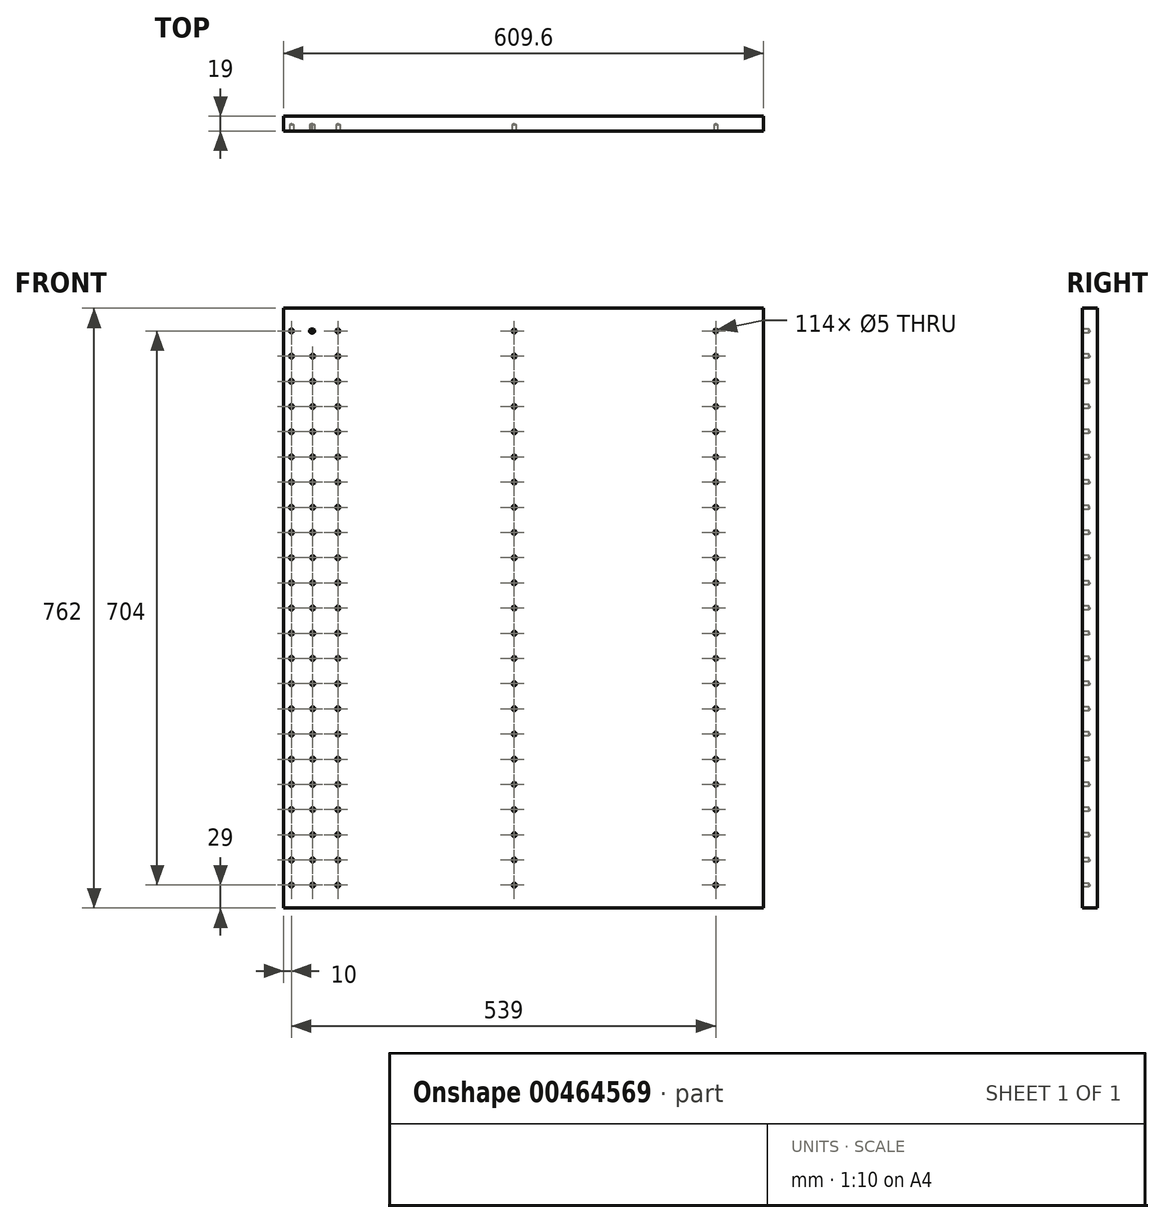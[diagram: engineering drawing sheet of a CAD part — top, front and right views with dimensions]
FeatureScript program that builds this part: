
annotation { "Feature Type Name" : "Feature", "Feature Type Description" : "" }
export const myFeature = defineFeature(function(context is Context, id is Id, definition is map)
    precondition{}
    {
        {
            var Q0;
            Q0=qCreatedBy(makeId("Front.planeOp"),FACE);
            var sketch = newSketch(context, id + "F0", { "sketchPlane" : qUnion([Q0])});
            skLineSegment(sketch, "E0.bottom", {"start": v(304.8, 381) * mm, "end": v(-304.8, 381) * mm});
            skLineSegment(sketch, "E0.top", {"start": v(304.8, -381) * mm, "end": v(-304.8, -381) * mm});
            skLineSegment(sketch, "E0.left", {"start": v(304.8, 381) * mm, "end": v(304.8, -381) * mm});
            skLineSegment(sketch, "E0.right", {"start": v(-304.8, 381) * mm, "end": v(-304.8, -381) * mm});
            skPoint(sketch, "E0.middle", {"position": v(0, 0) * mm});
            skSolve(sketch);
        }
        {
            var Q0;
            Q0=makeQuery(id+"F0.imprint","IMPRINT",FACE,{"disambiguationData":[TD([[makeQuery(id+"F0.imprint","IMPRINT",EDGE,{"derivedFrom":sQuery(id+"F0.wireOp",EDGE,"E0.bottom")}),1.0]])]});
            extrude(context, id + "F1", {"entities" : qUnion([Q0]), "depth" : 19 * mm});
        }
        {
            var Q0;
            Q0=makeQuery(id+"F1.opExtrude","CAP_FACE",FACE,{"disambiguationData":[OSD([sQuery(id+"F0.wireOp",EDGE,"E0.bottom"),sQuery(id+"F0.wireOp",EDGE,"E0.top"),sQuery(id+"F0.wireOp",EDGE,"E0.left"),sQuery(id+"F0.wireOp",EDGE,"E0.right")])],"isStart":false});
            var sketch = newSketch(context, id + "F2", { "sketchPlane" : qUnion([Q0])});
            skCircle(sketch, "E1", {"center": v(-294.8, 352) * mm, "radius": 2.5 * mm});
            skCircle(sketch, "E2.1.0.0", {"center": v(-267.8, 352) * mm, "radius": 2.5 * mm});
            skLineSegment(sketch, "E2.direction1", {"start": v(-294.8, 352) * mm, "end": v(-267.8, 352) * mm, "construction": true});
            skCircle(sketch, "E3.1.0.0", {"center": v(-235.8, 352) * mm, "radius": 2.5 * mm});
            skLineSegment(sketch, "E3.direction1", {"start": v(-267.8, 352) * mm, "end": v(-235.8, 352) * mm, "construction": true});
            skCircle(sketch, "E4.1.0.0", {"center": v(-11.8, 352) * mm, "radius": 2.5 * mm});
            skLineSegment(sketch, "E4.direction1", {"start": v(-235.8, 352) * mm, "end": v(-11.8, 352) * mm, "construction": true});
            skCircle(sketch, "E5.1.0.0", {"center": v(244.2, 352) * mm, "radius": 2.5 * mm});
            skLineSegment(sketch, "E5.direction1", {"start": v(-11.8, 352) * mm, "end": v(244.2, 352) * mm, "construction": true});
            skCircle(sketch, "E6.0.1.0", {"center": v(-11.8, 320) * mm, "radius": 2.5 * mm});
            skCircle(sketch, "E6.0.1.1", {"center": v(244.2, 320) * mm, "radius": 2.5 * mm});
            skCircle(sketch, "E6.0.1.2", {"center": v(-267.8, 320) * mm, "radius": 2.5 * mm});
            skCircle(sketch, "E6.0.1.3", {"center": v(-235.8, 320) * mm, "radius": 2.5 * mm});
            skCircle(sketch, "E6.0.1.4", {"center": v(-294.8, 320) * mm, "radius": 2.5 * mm});
            skCircle(sketch, "E6.0.2.0", {"center": v(-11.8, 288) * mm, "radius": 2.5 * mm});
            skCircle(sketch, "E6.0.2.1", {"center": v(244.2, 288) * mm, "radius": 2.5 * mm});
            skCircle(sketch, "E6.0.2.2", {"center": v(-267.8, 288) * mm, "radius": 2.5 * mm});
            skCircle(sketch, "E6.0.2.3", {"center": v(-235.8, 288) * mm, "radius": 2.5 * mm});
            skCircle(sketch, "E6.0.2.4", {"center": v(-294.8, 288) * mm, "radius": 2.5 * mm});
            skCircle(sketch, "E6.0.3.0", {"center": v(-11.8, 256) * mm, "radius": 2.5 * mm});
            skCircle(sketch, "E6.0.3.1", {"center": v(244.2, 256) * mm, "radius": 2.5 * mm});
            skCircle(sketch, "E6.0.3.2", {"center": v(-267.8, 256) * mm, "radius": 2.5 * mm});
            skCircle(sketch, "E6.0.3.3", {"center": v(-235.8, 256) * mm, "radius": 2.5 * mm});
            skCircle(sketch, "E6.0.3.4", {"center": v(-294.8, 256) * mm, "radius": 2.5 * mm});
            skCircle(sketch, "E6.0.4.0", {"center": v(-11.8, 224) * mm, "radius": 2.5 * mm});
            skCircle(sketch, "E6.0.4.1", {"center": v(244.2, 224) * mm, "radius": 2.5 * mm});
            skCircle(sketch, "E6.0.4.2", {"center": v(-267.8, 224) * mm, "radius": 2.5 * mm});
            skCircle(sketch, "E6.0.4.3", {"center": v(-235.8, 224) * mm, "radius": 2.5 * mm});
            skCircle(sketch, "E6.0.4.4", {"center": v(-294.8, 224) * mm, "radius": 2.5 * mm});
            skCircle(sketch, "E6.0.5.0", {"center": v(-11.8, 192) * mm, "radius": 2.5 * mm});
            skCircle(sketch, "E6.0.5.1", {"center": v(244.2, 192) * mm, "radius": 2.5 * mm});
            skCircle(sketch, "E6.0.5.2", {"center": v(-267.8, 192) * mm, "radius": 2.5 * mm});
            skCircle(sketch, "E6.0.5.3", {"center": v(-235.8, 192) * mm, "radius": 2.5 * mm});
            skCircle(sketch, "E6.0.5.4", {"center": v(-294.8, 192) * mm, "radius": 2.5 * mm});
            skCircle(sketch, "E6.0.6.0", {"center": v(-11.8, 160) * mm, "radius": 2.5 * mm});
            skCircle(sketch, "E6.0.6.1", {"center": v(244.2, 160) * mm, "radius": 2.5 * mm});
            skCircle(sketch, "E6.0.6.2", {"center": v(-267.8, 160) * mm, "radius": 2.5 * mm});
            skCircle(sketch, "E6.0.6.3", {"center": v(-235.8, 160) * mm, "radius": 2.5 * mm});
            skCircle(sketch, "E6.0.6.4", {"center": v(-294.8, 160) * mm, "radius": 2.5 * mm});
            skCircle(sketch, "E6.0.7.0", {"center": v(-11.8, 128) * mm, "radius": 2.5 * mm});
            skCircle(sketch, "E6.0.7.1", {"center": v(244.2, 128) * mm, "radius": 2.5 * mm});
            skCircle(sketch, "E6.0.7.2", {"center": v(-267.8, 128) * mm, "radius": 2.5 * mm});
            skCircle(sketch, "E6.0.7.3", {"center": v(-235.8, 128) * mm, "radius": 2.5 * mm});
            skCircle(sketch, "E6.0.7.4", {"center": v(-294.8, 128) * mm, "radius": 2.5 * mm});
            skCircle(sketch, "E6.0.8.0", {"center": v(-11.8, 96) * mm, "radius": 2.5 * mm});
            skCircle(sketch, "E6.0.8.1", {"center": v(244.2, 96) * mm, "radius": 2.5 * mm});
            skCircle(sketch, "E6.0.8.2", {"center": v(-267.8, 96) * mm, "radius": 2.5 * mm});
            skCircle(sketch, "E6.0.8.3", {"center": v(-235.8, 96) * mm, "radius": 2.5 * mm});
            skCircle(sketch, "E6.0.8.4", {"center": v(-294.8, 96) * mm, "radius": 2.5 * mm});
            skCircle(sketch, "E6.0.9.0", {"center": v(-11.8, 64) * mm, "radius": 2.5 * mm});
            skCircle(sketch, "E6.0.9.1", {"center": v(244.2, 64) * mm, "radius": 2.5 * mm});
            skCircle(sketch, "E6.0.9.2", {"center": v(-267.8, 64) * mm, "radius": 2.5 * mm});
            skCircle(sketch, "E6.0.9.3", {"center": v(-235.8, 64) * mm, "radius": 2.5 * mm});
            skCircle(sketch, "E6.0.9.4", {"center": v(-294.8, 64) * mm, "radius": 2.5 * mm});
            skCircle(sketch, "E6.0.10.0", {"center": v(-11.8, 32) * mm, "radius": 2.5 * mm});
            skCircle(sketch, "E6.0.10.1", {"center": v(244.2, 32) * mm, "radius": 2.5 * mm});
            skCircle(sketch, "E6.0.10.2", {"center": v(-267.8, 32) * mm, "radius": 2.5 * mm});
            skCircle(sketch, "E6.0.10.3", {"center": v(-235.8, 32) * mm, "radius": 2.5 * mm});
            skCircle(sketch, "E6.0.10.4", {"center": v(-294.8, 32) * mm, "radius": 2.5 * mm});
            skCircle(sketch, "E6.0.11.0", {"center": v(-11.8, 0) * mm, "radius": 2.5 * mm});
            skCircle(sketch, "E6.0.11.1", {"center": v(244.2, 0) * mm, "radius": 2.5 * mm});
            skCircle(sketch, "E6.0.11.2", {"center": v(-267.8, 0) * mm, "radius": 2.5 * mm});
            skCircle(sketch, "E6.0.11.3", {"center": v(-235.8, 0) * mm, "radius": 2.5 * mm});
            skCircle(sketch, "E6.0.11.4", {"center": v(-294.8, 0) * mm, "radius": 2.5 * mm});
            skCircle(sketch, "E6.0.12.0", {"center": v(-11.8, -32) * mm, "radius": 2.5 * mm});
            skCircle(sketch, "E6.0.12.1", {"center": v(244.2, -32) * mm, "radius": 2.5 * mm});
            skCircle(sketch, "E6.0.12.2", {"center": v(-267.8, -32) * mm, "radius": 2.5 * mm});
            skCircle(sketch, "E6.0.12.3", {"center": v(-235.8, -32) * mm, "radius": 2.5 * mm});
            skCircle(sketch, "E6.0.12.4", {"center": v(-294.8, -32) * mm, "radius": 2.5 * mm});
            skCircle(sketch, "E6.0.13.0", {"center": v(-11.8, -64) * mm, "radius": 2.5 * mm});
            skCircle(sketch, "E6.0.13.1", {"center": v(244.2, -64) * mm, "radius": 2.5 * mm});
            skCircle(sketch, "E6.0.13.2", {"center": v(-267.8, -64) * mm, "radius": 2.5 * mm});
            skCircle(sketch, "E6.0.13.3", {"center": v(-235.8, -64) * mm, "radius": 2.5 * mm});
            skCircle(sketch, "E6.0.13.4", {"center": v(-294.8, -64) * mm, "radius": 2.5 * mm});
            skCircle(sketch, "E6.0.14.0", {"center": v(-11.8, -96) * mm, "radius": 2.5 * mm});
            skCircle(sketch, "E6.0.14.1", {"center": v(244.2, -96) * mm, "radius": 2.5 * mm});
            skCircle(sketch, "E6.0.14.2", {"center": v(-267.8, -96) * mm, "radius": 2.5 * mm});
            skCircle(sketch, "E6.0.14.3", {"center": v(-235.8, -96) * mm, "radius": 2.5 * mm});
            skCircle(sketch, "E6.0.14.4", {"center": v(-294.8, -96) * mm, "radius": 2.5 * mm});
            skCircle(sketch, "E6.0.15.0", {"center": v(-11.8, -128) * mm, "radius": 2.5 * mm});
            skCircle(sketch, "E6.0.15.1", {"center": v(244.2, -128) * mm, "radius": 2.5 * mm});
            skCircle(sketch, "E6.0.15.2", {"center": v(-267.8, -128) * mm, "radius": 2.5 * mm});
            skCircle(sketch, "E6.0.15.3", {"center": v(-235.8, -128) * mm, "radius": 2.5 * mm});
            skCircle(sketch, "E6.0.15.4", {"center": v(-294.8, -128) * mm, "radius": 2.5 * mm});
            skCircle(sketch, "E6.0.16.0", {"center": v(-11.8, -160) * mm, "radius": 2.5 * mm});
            skCircle(sketch, "E6.0.16.1", {"center": v(244.2, -160) * mm, "radius": 2.5 * mm});
            skCircle(sketch, "E6.0.16.2", {"center": v(-267.8, -160) * mm, "radius": 2.5 * mm});
            skCircle(sketch, "E6.0.16.3", {"center": v(-235.8, -160) * mm, "radius": 2.5 * mm});
            skCircle(sketch, "E6.0.16.4", {"center": v(-294.8, -160) * mm, "radius": 2.5 * mm});
            skCircle(sketch, "E6.0.17.0", {"center": v(-11.8, -192) * mm, "radius": 2.5 * mm});
            skCircle(sketch, "E6.0.17.1", {"center": v(244.2, -192) * mm, "radius": 2.5 * mm});
            skCircle(sketch, "E6.0.17.2", {"center": v(-267.8, -192) * mm, "radius": 2.5 * mm});
            skCircle(sketch, "E6.0.17.3", {"center": v(-235.8, -192) * mm, "radius": 2.5 * mm});
            skCircle(sketch, "E6.0.17.4", {"center": v(-294.8, -192) * mm, "radius": 2.5 * mm});
            skCircle(sketch, "E6.0.18.0", {"center": v(-11.8, -224) * mm, "radius": 2.5 * mm});
            skCircle(sketch, "E6.0.18.1", {"center": v(244.2, -224) * mm, "radius": 2.5 * mm});
            skCircle(sketch, "E6.0.18.2", {"center": v(-267.8, -224) * mm, "radius": 2.5 * mm});
            skCircle(sketch, "E6.0.18.3", {"center": v(-235.8, -224) * mm, "radius": 2.5 * mm});
            skCircle(sketch, "E6.0.18.4", {"center": v(-294.8, -224) * mm, "radius": 2.5 * mm});
            skCircle(sketch, "E6.0.19.0", {"center": v(-11.8, -256) * mm, "radius": 2.5 * mm});
            skCircle(sketch, "E6.0.19.1", {"center": v(244.2, -256) * mm, "radius": 2.5 * mm});
            skCircle(sketch, "E6.0.19.2", {"center": v(-267.8, -256) * mm, "radius": 2.5 * mm});
            skCircle(sketch, "E6.0.19.3", {"center": v(-235.8, -256) * mm, "radius": 2.5 * mm});
            skCircle(sketch, "E6.0.19.4", {"center": v(-294.8, -256) * mm, "radius": 2.5 * mm});
            skCircle(sketch, "E6.0.20.0", {"center": v(-11.8, -288) * mm, "radius": 2.5 * mm});
            skCircle(sketch, "E6.0.20.1", {"center": v(244.2, -288) * mm, "radius": 2.5 * mm});
            skCircle(sketch, "E6.0.20.2", {"center": v(-267.8, -288) * mm, "radius": 2.5 * mm});
            skCircle(sketch, "E6.0.20.3", {"center": v(-235.8, -288) * mm, "radius": 2.5 * mm});
            skCircle(sketch, "E6.0.20.4", {"center": v(-294.8, -288) * mm, "radius": 2.5 * mm});
            skCircle(sketch, "E6.0.21.0", {"center": v(-11.8, -320) * mm, "radius": 2.5 * mm});
            skCircle(sketch, "E6.0.21.1", {"center": v(244.2, -320) * mm, "radius": 2.5 * mm});
            skCircle(sketch, "E6.0.21.2", {"center": v(-267.8, -320) * mm, "radius": 2.5 * mm});
            skCircle(sketch, "E6.0.21.3", {"center": v(-235.8, -320) * mm, "radius": 2.5 * mm});
            skCircle(sketch, "E6.0.21.4", {"center": v(-294.8, -320) * mm, "radius": 2.5 * mm});
            skCircle(sketch, "E6.0.22.0", {"center": v(-11.8, -352) * mm, "radius": 2.5 * mm});
            skCircle(sketch, "E6.0.22.1", {"center": v(244.2, -352) * mm, "radius": 2.5 * mm});
            skCircle(sketch, "E6.0.22.2", {"center": v(-267.8, -352) * mm, "radius": 2.5 * mm});
            skCircle(sketch, "E6.0.22.3", {"center": v(-235.8, -352) * mm, "radius": 2.5 * mm});
            skCircle(sketch, "E6.0.22.4", {"center": v(-294.8, -352) * mm, "radius": 2.5 * mm});
            skLineSegment(sketch, "E6.direction1", {"start": v(-294.8, 352) * mm, "end": v(-269.4, 352) * mm, "construction": true});
            skLineSegment(sketch, "E6.direction2", {"start": v(-294.8, 352) * mm, "end": v(-294.8, 320) * mm, "construction": true});
            skSolve(sketch);
        }
        {
            var Q0;
            Q0=sQuery(id+"F2.wireOp",VERTEX,"E6.0.10.3.center");
            var Q1;
            Q1=sQuery(id+"F2.wireOp",VERTEX,"E6.0.4.3.center");
            var Q2;
            Q2=sQuery(id+"F2.wireOp",VERTEX,"E6.0.15.0.center");
            var Q3;
            Q3=sQuery(id+"F2.wireOp",VERTEX,"E2.direction1.end");
            var Q4;
            Q4=sQuery(id+"F2.wireOp",VERTEX,"E6.0.8.0.center");
            var Q5;
            Q5=sQuery(id+"F2.wireOp",VERTEX,"E6.0.11.0.center");
            var Q6;
            Q6=sQuery(id+"F2.wireOp",VERTEX,"E6.0.22.2.center");
            var Q7;
            Q7=sQuery(id+"F2.wireOp",VERTEX,"E6.0.3.2.center");
            var Q8;
            Q8=sQuery(id+"F2.wireOp",VERTEX,"E6.0.15.4.center");
            var Q9;
            Q9=sQuery(id+"F2.wireOp",VERTEX,"E6.0.7.3.center");
            var Q10;
            Q10=sQuery(id+"F2.wireOp",VERTEX,"E6.0.3.4.center");
            var Q11;
            Q11=sQuery(id+"F2.wireOp",VERTEX,"E6.0.7.0.center");
            var Q12;
            Q12=sQuery(id+"F2.wireOp",VERTEX,"E6.0.16.4.center");
            var Q13;
            Q13=sQuery(id+"F2.wireOp",VERTEX,"E6.0.17.4.center");
            var Q14;
            Q14=sQuery(id+"F2.wireOp",VERTEX,"E6.0.3.3.center");
            var Q15;
            Q15=sQuery(id+"F2.wireOp",VERTEX,"E6.0.9.4.center");
            var Q16;
            Q16=sQuery(id+"F2.wireOp",VERTEX,"E6.0.10.4.center");
            var Q17;
            Q17=sQuery(id+"F2.wireOp",VERTEX,"E6.0.18.3.center");
            var Q18;
            Q18=sQuery(id+"F2.wireOp",VERTEX,"E6.direction2.start");
            var Q19;
            Q19=sQuery(id+"F2.wireOp",VERTEX,"E6.0.7.4.center");
            var Q20;
            Q20=sQuery(id+"F2.wireOp",VERTEX,"E6.0.14.0.center");
            var Q21;
            Q21=sQuery(id+"F2.wireOp",VERTEX,"E6.0.6.4.center");
            var Q22;
            Q22=sQuery(id+"F2.wireOp",VERTEX,"E6.0.2.3.center");
            var Q23;
            Q23=sQuery(id+"F2.wireOp",VERTEX,"E6.0.2.0.center");
            var Q24;
            Q24=sQuery(id+"F2.wireOp",VERTEX,"E6.direction1.end");
            var Q25;
            Q25=sQuery(id+"F2.wireOp",VERTEX,"E6.0.16.3.center");
            var Q26;
            Q26=sQuery(id+"F2.wireOp",VERTEX,"E6.0.8.3.center");
            var Q27;
            Q27=sQuery(id+"F2.wireOp",VERTEX,"E6.0.22.0.center");
            var Q28;
            Q28=sQuery(id+"F2.wireOp",VERTEX,"E6.0.19.3.center");
            var Q29;
            Q29=sQuery(id+"F2.wireOp",VERTEX,"E6.0.14.2.center");
            var Q30;
            Q30=sQuery(id+"F2.wireOp",VERTEX,"E6.0.4.2.center");
            var Q31;
            Q31=sQuery(id+"F2.wireOp",VERTEX,"E6.0.20.0.center");
            var Q32;
            Q32=sQuery(id+"F2.wireOp",VERTEX,"E6.0.21.3.center");
            var Q33;
            Q33=sQuery(id+"F2.wireOp",VERTEX,"E6.0.7.2.center");
            var Q34;
            Q34=sQuery(id+"F2.wireOp",VERTEX,"E6.0.5.0.center");
            var Q35;
            Q35=sQuery(id+"F2.wireOp",VERTEX,"E6.0.4.0.center");
            var Q36;
            Q36=sQuery(id+"F2.wireOp",VERTEX,"E6.0.18.4.center");
            var Q37;
            Q37=sQuery(id+"F2.wireOp",VERTEX,"E6.direction2.end");
            var Q38;
            Q38=sQuery(id+"F2.wireOp",VERTEX,"E6.0.2.4.center");
            var Q39;
            Q39=sQuery(id+"F2.wireOp",VERTEX,"E6.0.15.3.center");
            var Q40;
            Q40=sQuery(id+"F2.wireOp",VERTEX,"E6.0.6.3.center");
            var Q41;
            Q41=sQuery(id+"F2.wireOp",VERTEX,"E4.direction1.end");
            var Q42;
            Q42=sQuery(id+"F2.wireOp",VERTEX,"E6.0.19.4.center");
            var Q43;
            Q43=sQuery(id+"F2.wireOp",VERTEX,"E6.0.11.3.center");
            var Q44;
            Q44=sQuery(id+"F2.wireOp",VERTEX,"E6.0.5.4.center");
            var Q45;
            Q45=sQuery(id+"F2.wireOp",VERTEX,"E6.0.17.3.center");
            var Q46;
            Q46=sQuery(id+"F2.wireOp",VERTEX,"E6.0.1.0.center");
            var Q47;
            Q47=sQuery(id+"F2.wireOp",VERTEX,"E6.0.20.4.center");
            var Q48;
            Q48=sQuery(id+"F2.wireOp",VERTEX,"E6.0.21.0.center");
            var Q49;
            Q49=sQuery(id+"F2.wireOp",VERTEX,"E6.0.17.2.center");
            var Q50;
            Q50=sQuery(id+"F2.wireOp",VERTEX,"E6.0.21.4.center");
            var Q51;
            Q51=sQuery(id+"F2.wireOp",VERTEX,"E6.0.17.0.center");
            var Q52;
            Q52=sQuery(id+"F2.wireOp",VERTEX,"E6.0.3.0.center");
            var Q53;
            Q53=sQuery(id+"F2.wireOp",VERTEX,"E6.0.12.2.center");
            var Q54;
            Q54=sQuery(id+"F2.wireOp",VERTEX,"E6.0.8.2.center");
            var Q55;
            Q55=sQuery(id+"F2.wireOp",VERTEX,"E6.0.6.2.center");
            var Q56;
            Q56=sQuery(id+"F2.wireOp",VERTEX,"E6.0.14.4.center");
            var Q57;
            Q57=sQuery(id+"F2.wireOp",VERTEX,"E6.0.9.3.center");
            var Q58;
            Q58=sQuery(id+"F2.wireOp",VERTEX,"E6.0.13.0.center");
            var Q59;
            Q59=sQuery(id+"F2.wireOp",VERTEX,"E6.0.12.4.center");
            var Q60;
            Q60=sQuery(id+"F2.wireOp",VERTEX,"E6.0.22.4.center");
            var Q61;
            Q61=sQuery(id+"F2.wireOp",VERTEX,"E6.0.1.2.center");
            var Q62;
            Q62=sQuery(id+"F2.wireOp",VERTEX,"E6.0.11.4.center");
            var Q63;
            Q63=sQuery(id+"F2.wireOp",VERTEX,"E6.0.6.0.center");
            var Q64;
            Q64=sQuery(id+"F2.wireOp",VERTEX,"E6.0.16.0.center");
            var Q65;
            Q65=sQuery(id+"F2.wireOp",VERTEX,"E3.1.0.0.center");
            var Q66;
            Q66=sQuery(id+"F2.wireOp",VERTEX,"E6.0.9.0.center");
            var Q67;
            Q67=sQuery(id+"F2.wireOp",VERTEX,"E6.0.9.2.center");
            var Q68;
            Q68=sQuery(id+"F2.wireOp",VERTEX,"E6.0.18.2.center");
            var Q69;
            Q69=sQuery(id+"F2.wireOp",VERTEX,"E6.0.11.2.center");
            var Q70;
            Q70=sQuery(id+"F2.wireOp",VERTEX,"E6.0.2.2.center");
            var Q71;
            Q71=sQuery(id+"F2.wireOp",VERTEX,"E6.0.13.3.center");
            var Q72;
            Q72=sQuery(id+"F2.wireOp",VERTEX,"E6.0.15.2.center");
            var Q73;
            Q73=sQuery(id+"F2.wireOp",VERTEX,"E6.0.19.0.center");
            var Q74;
            Q74=sQuery(id+"F2.wireOp",VERTEX,"E6.0.20.3.center");
            var Q75;
            Q75=sQuery(id+"F2.wireOp",VERTEX,"E6.0.10.0.center");
            var Q76;
            Q76=sQuery(id+"F2.wireOp",VERTEX,"E6.0.8.4.center");
            var Q77;
            Q77=sQuery(id+"F2.wireOp",VERTEX,"E6.0.16.2.center");
            var Q78;
            Q78=sQuery(id+"F2.wireOp",VERTEX,"E6.0.13.4.center");
            var Q79;
            Q79=sQuery(id+"F2.wireOp",VERTEX,"E6.0.10.2.center");
            var Q80;
            Q80=sQuery(id+"F2.wireOp",VERTEX,"E6.0.19.2.center");
            var Q81;
            Q81=sQuery(id+"F2.wireOp",VERTEX,"E6.0.14.3.center");
            var Q82;
            Q82=sQuery(id+"F2.wireOp",VERTEX,"E6.0.22.3.center");
            var Q83;
            Q83=sQuery(id+"F2.wireOp",VERTEX,"E6.0.21.2.center");
            var Q84;
            Q84=sQuery(id+"F2.wireOp",VERTEX,"E6.0.20.2.center");
            var Q85;
            Q85=sQuery(id+"F2.wireOp",VERTEX,"E6.0.12.3.center");
            var Q86;
            Q86=sQuery(id+"F2.wireOp",VERTEX,"E6.0.13.2.center");
            var Q87;
            Q87=sQuery(id+"F2.wireOp",VERTEX,"E6.0.4.4.center");
            var Q88;
            Q88=sQuery(id+"F2.wireOp",VERTEX,"E6.0.1.3.center");
            var Q89;
            Q89=sQuery(id+"F2.wireOp",VERTEX,"E6.0.18.0.center");
            var Q90;
            Q90=sQuery(id+"F2.wireOp",VERTEX,"E6.0.5.3.center");
            var Q91;
            Q91=sQuery(id+"F2.wireOp",VERTEX,"E6.0.12.0.center");
            var Q92;
            Q92=sQuery(id+"F2.wireOp",VERTEX,"E6.0.5.2.center");
            var Q93;
            Q93=makeQuery(id+"F1.opExtrude","SWEPT_BODY",BODY,{"disambiguationData":[OSD([sQuery(id+"F0.wireOp",EDGE,"E0.bottom"),sQuery(id+"F0.wireOp",EDGE,"E0.top"),sQuery(id+"F0.wireOp",EDGE,"E0.left"),sQuery(id+"F0.wireOp",EDGE,"E0.right")])]});
            hole(context, id + "F3", {"style" : HoleStyle.SIMPLE, "endStyle" : HoleEndStyle.BLIND, "holeDiameter" : 5 * mm, "holeDepth" : 8 * mm, "isTappedThrough" : true, "tappedDepth" : 12.7 * mm, "tapClearance" : 3, "startFromSketch" : true, "locations" : qUnion([Q0, Q1, Q2, Q3, Q4, Q5, Q6, Q7, Q8, Q9, Q10, Q11, Q12, Q13, Q14, Q15, Q16, Q17, Q18, Q19, Q20, Q21, Q22, Q23, Q24, Q25, Q26, Q27, Q28, Q29, Q30, Q31, Q32, Q33, Q34, Q35, Q36, Q37, Q38, Q39, Q40, Q41, Q42, Q43, Q44, Q45, Q46, Q47, Q48, Q49, Q50, Q51, Q52, Q53, Q54, Q55, Q56, Q57, Q58, Q59, Q60, Q61, Q62, Q63, Q64, Q65, Q66, Q67, Q68, Q69, Q70, Q71, Q72, Q73, Q74, Q75, Q76, Q77, Q78, Q79, Q80, Q81, Q82, Q83, Q84, Q85, Q86, Q87, Q88, Q89, Q90, Q91, Q92]), "scope" : qUnion([Q93])});
        }
        {
            var Q0;
            Q0=sQuery(id+"F2.wireOp",VERTEX,"E6.0.2.1.center");
            var Q1;
            Q1=sQuery(id+"F2.wireOp",VERTEX,"E6.0.16.1.center");
            var Q2;
            Q2=sQuery(id+"F2.wireOp",VERTEX,"E6.0.10.1.center");
            var Q3;
            Q3=sQuery(id+"F2.wireOp",VERTEX,"E5.direction1.end");
            var Q4;
            Q4=sQuery(id+"F2.wireOp",VERTEX,"E6.0.19.1.center");
            var Q5;
            Q5=sQuery(id+"F2.wireOp",VERTEX,"E6.0.21.1.center");
            var Q6;
            Q6=sQuery(id+"F2.wireOp",VERTEX,"E6.0.18.1.center");
            var Q7;
            Q7=sQuery(id+"F2.wireOp",VERTEX,"E6.0.11.1.center");
            var Q8;
            Q8=sQuery(id+"F2.wireOp",VERTEX,"E6.0.12.1.center");
            var Q9;
            Q9=sQuery(id+"F2.wireOp",VERTEX,"E6.0.15.1.center");
            var Q10;
            Q10=sQuery(id+"F2.wireOp",VERTEX,"E6.0.4.1.center");
            var Q11;
            Q11=sQuery(id+"F2.wireOp",VERTEX,"E6.0.14.1.center");
            var Q12;
            Q12=sQuery(id+"F2.wireOp",VERTEX,"E6.0.17.1.center");
            var Q13;
            Q13=sQuery(id+"F2.wireOp",VERTEX,"E6.0.1.1.center");
            var Q14;
            Q14=sQuery(id+"F2.wireOp",VERTEX,"E6.0.3.1.center");
            var Q15;
            Q15=sQuery(id+"F2.wireOp",VERTEX,"E6.0.5.1.center");
            var Q16;
            Q16=sQuery(id+"F2.wireOp",VERTEX,"E6.0.7.1.center");
            var Q17;
            Q17=sQuery(id+"F2.wireOp",VERTEX,"E6.0.9.1.center");
            var Q18;
            Q18=sQuery(id+"F2.wireOp",VERTEX,"E6.0.20.1.center");
            var Q19;
            Q19=sQuery(id+"F2.wireOp",VERTEX,"E6.0.8.1.center");
            var Q20;
            Q20=sQuery(id+"F2.wireOp",VERTEX,"E6.0.13.1.center");
            var Q21;
            Q21=sQuery(id+"F2.wireOp",VERTEX,"E6.0.6.1.center");
            var Q22;
            Q22=sQuery(id+"F2.wireOp",VERTEX,"E6.0.22.1.center");
            var Q23;
            Q23=makeQuery(id+"F1.opExtrude","SWEPT_BODY",BODY,{"disambiguationData":[OSD([sQuery(id+"F0.wireOp",EDGE,"E0.bottom"),sQuery(id+"F0.wireOp",EDGE,"E0.top"),sQuery(id+"F0.wireOp",EDGE,"E0.left"),sQuery(id+"F0.wireOp",EDGE,"E0.right")])]});
            hole(context, id + "F4", {"style" : HoleStyle.SIMPLE, "endStyle" : HoleEndStyle.BLIND, "holeDiameter" : 5 * mm, "holeDepth" : 8 * mm, "isTappedThrough" : true, "tappedDepth" : 12.7 * mm, "tapClearance" : 3, "startFromSketch" : true, "locations" : qUnion([Q0, Q1, Q2, Q3, Q4, Q5, Q6, Q7, Q8, Q9, Q10, Q11, Q12, Q13, Q14, Q15, Q16, Q17, Q18, Q19, Q20, Q21, Q22]), "scope" : qUnion([Q23])});
        }
    });
